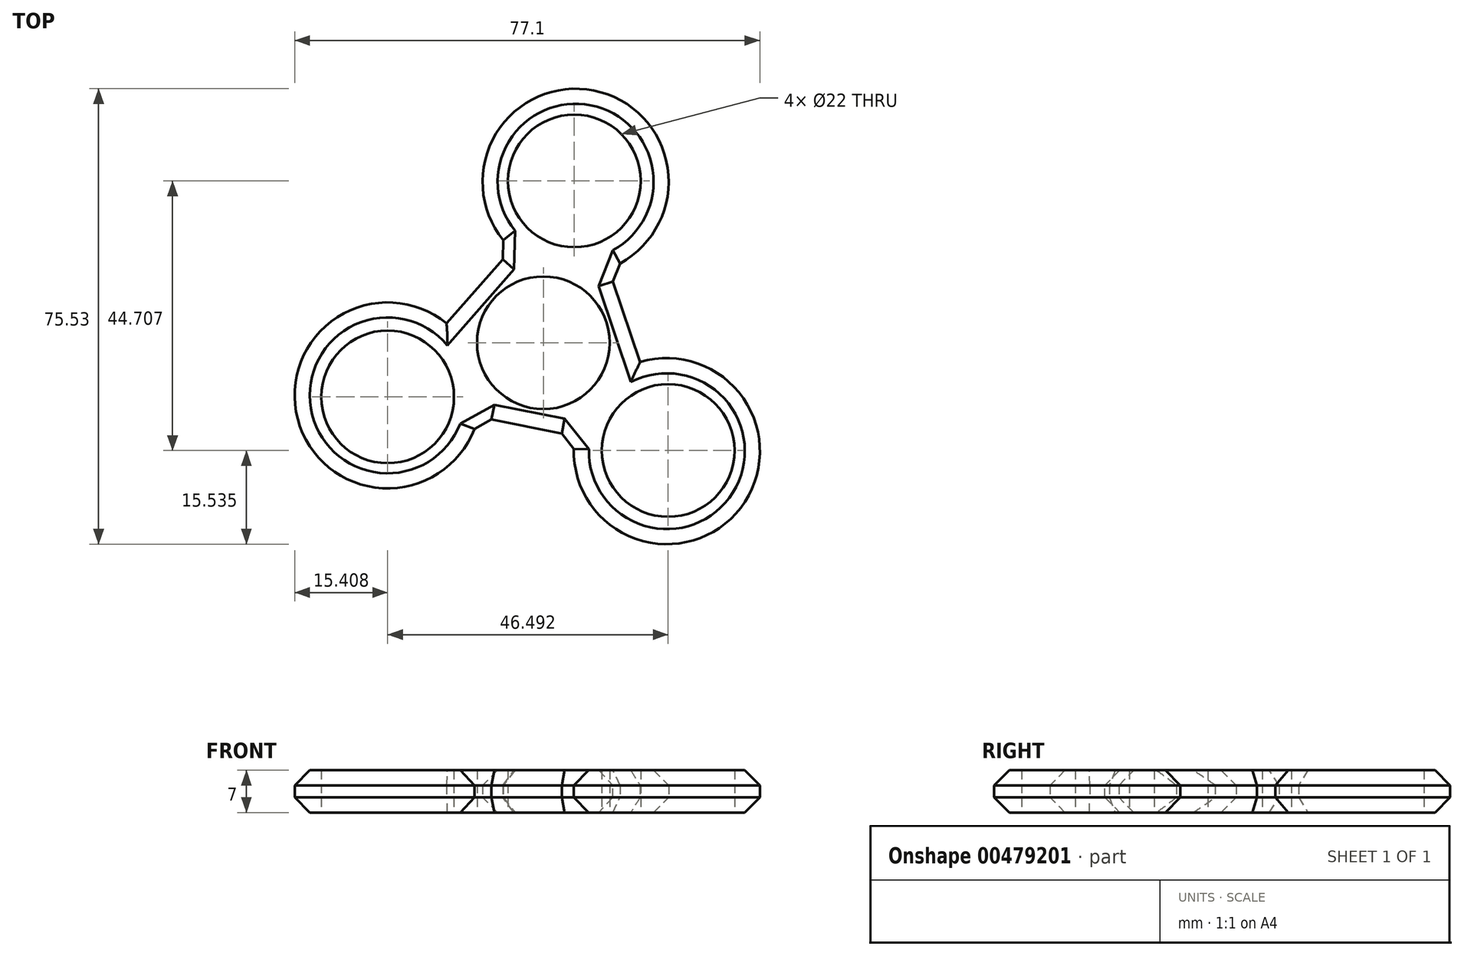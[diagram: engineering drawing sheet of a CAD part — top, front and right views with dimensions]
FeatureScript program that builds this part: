
annotation { "Feature Type Name" : "Feature", "Feature Type Description" : "" }
export const myFeature = defineFeature(function(context is Context, id is Id, definition is map)
    precondition{}
    {
        {
            var Q0;
            Q0=qCreatedBy(makeId("Top.planeOp"),FACE);
            var sketch = newSketch(context, id + "F0", { "sketchPlane" : qUnion([Q0])});
            skCircle(sketch, "E0", {"center": v(0, 0) * mm, "radius": 11 * mm});
            skCircle(sketch, "E1.cCircle", {"center": v(0, 0) * mm, "radius": 14.17 * mm, "construction": true});
            skLineSegment(sketch, "E1.0", {"start": v(10.8, 12.29) * mm, "end": v(16.04, -3.2) * mm});
            skLineSegment(sketch, "E1.1", {"start": v(16.04, -3.2) * mm, "end": v(5.24, -15.5) * mm});
            skLineSegment(sketch, "E1.2", {"start": v(5.24, -15.5) * mm, "end": v(-10.8, -12.29) * mm});
            skLineSegment(sketch, "E1.3", {"start": v(-10.8, -12.29) * mm, "end": v(-16.04, 3.2) * mm});
            skLineSegment(sketch, "E1.4", {"start": v(-16.04, 3.2) * mm, "end": v(-5.24, 15.5) * mm});
            skLineSegment(sketch, "E1.5", {"start": v(-5.24, 15.5) * mm, "end": v(10.8, 12.29) * mm});
            skPoint(sketch, "E1.0.midPoint", {"position": v(13.42, 4.54) * mm});
            skCircle(sketch, "E2", {"center": v(5.13, 26.84) * mm, "radius": 11 * mm});
            skCircle(sketch, "E3.1.0", {"center": v(-25.81, -8.98) * mm, "radius": 11 * mm});
            skCircle(sketch, "E3.2.0", {"center": v(20.68, -17.87) * mm, "radius": 11 * mm});
            skArc(sketch, "E4", {"start": v(-16.04, 3.2) * mm, "mid": v(-40.41, -13.67) * mm, "end": v(-10.8, -12.29) * mm});
            skArc(sketch, "E5.1.0", {"start": v(5.24, -15.5) * mm, "mid": v(32.04, -28.16) * mm, "end": v(16.04, -3.2) * mm});
            skArc(sketch, "E5.2.0", {"start": v(10.8, 12.29) * mm, "mid": v(8.37, 41.83) * mm, "end": v(-5.24, 15.5) * mm});
            skSolve(sketch);
        }
        {
            var Q0;
            Q0 = qSketchRegion(id + "F0", true);
            extrude(context, id + "F1", {"entities" : qUnion([Q0]), "depth" : 7 * mm});
        }
        {
            var Q0;
            Q0=makeQuery(id+"F1.opExtrude","CAP_EDGE",EDGE,{"disambiguationData":[OSD([sQuery(id+"F0.wireOp",EDGE,"E1.4")])],"isStart":false});
            var Q1;
            Q1=makeQuery(id+"F1.opExtrude","CAP_EDGE",EDGE,{"disambiguationData":[OSD([sQuery(id+"F0.wireOp",EDGE,"E1.4")])],"isStart":true});
            var Q2;
            Q2=makeQuery(id+"F1.opExtrude","CAP_EDGE",EDGE,{"disambiguationData":[OSD([sQuery(id+"F0.wireOp",EDGE,"E1.0")])],"isStart":false});
            var Q3;
            Q3=makeQuery(id+"F1.opExtrude","CAP_EDGE",EDGE,{"disambiguationData":[OSD([sQuery(id+"F0.wireOp",EDGE,"E1.0")])],"isStart":true});
            var Q4;
            Q4=makeQuery(id+"F1.opExtrude","SWEPT_FACE",FACE,{"disambiguationData":[OSD([sQuery(id+"F0.wireOp",EDGE,"E1.2")])]});
            var Q5;
            Q5=makeQuery(id+"F1.opExtrude","SWEPT_FACE",FACE,{"disambiguationData":[OSD([sQuery(id+"F0.wireOp",EDGE,"E5.2.0")])]});
            chamfer(context, id + "F2", {"entities" : qUnion([Q0, Q1, Q2, Q3, Q4, Q5]), "width" : 2.5 * mm, "tangentPropagation" : true});
        }
    });
